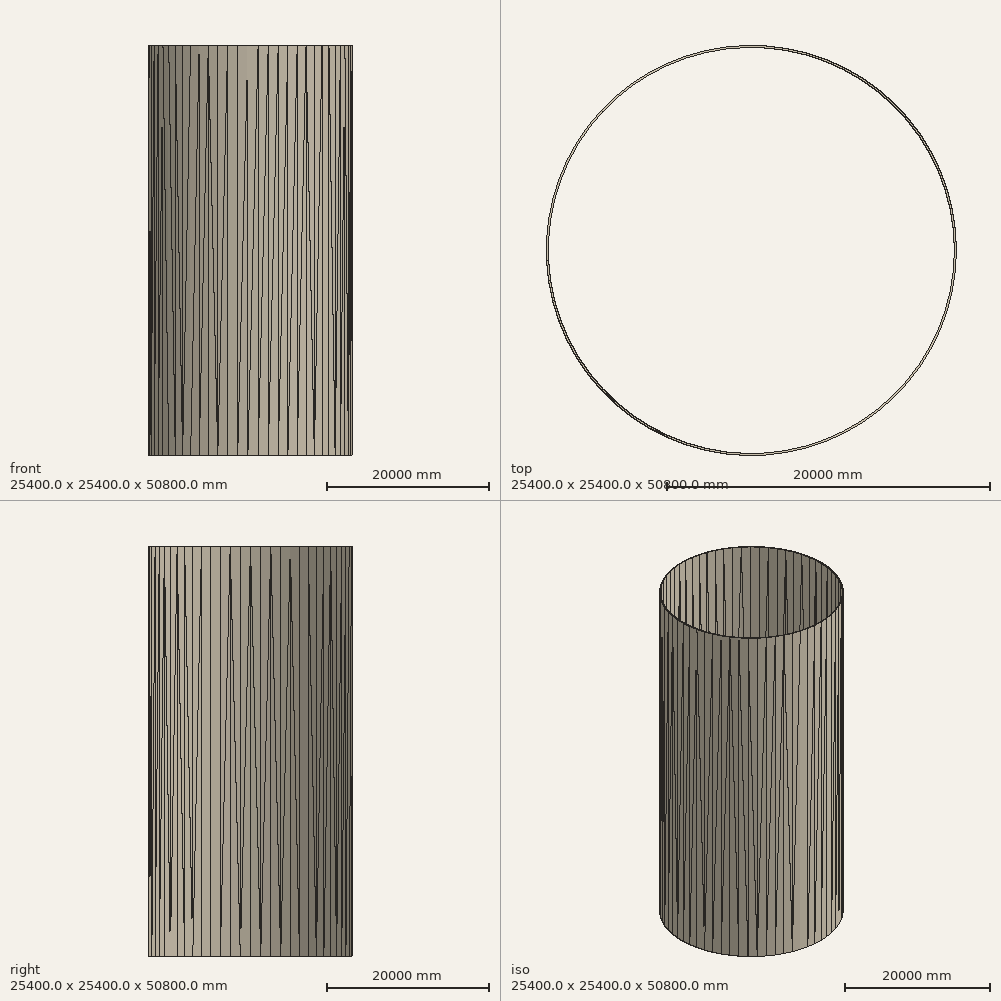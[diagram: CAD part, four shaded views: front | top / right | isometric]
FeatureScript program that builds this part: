
annotation { "Feature Type Name" : "Feature", "Feature Type Description" : "" }
export const myFeature = defineFeature(function(context is Context, id is Id, definition is map)
    precondition{}
    {
        {
            var Q0;
            Q0=qCreatedBy(makeId("Top.planeOp"),FACE);
            var sketch = newSketch(context, id + "F0", { "sketchPlane" : qUnion([Q0])});
            skCircle(sketch, "E0", {"center": v(0, 0) * mm, "radius": 12700 * mm});
            skCircle(sketch, "E1", {"center": v(0, 0) * mm, "radius": 12573 * mm});
            skSolve(sketch);
        }
        {
            var Q0;
            Q0 = qSketchRegion(id + "F0", true);
            extrude(context, id + "F1", {"entities" : qUnion([Q0]), "depth" : 50800 * mm, "offsetDistance" : 25.4 * mm});
        }
    });
